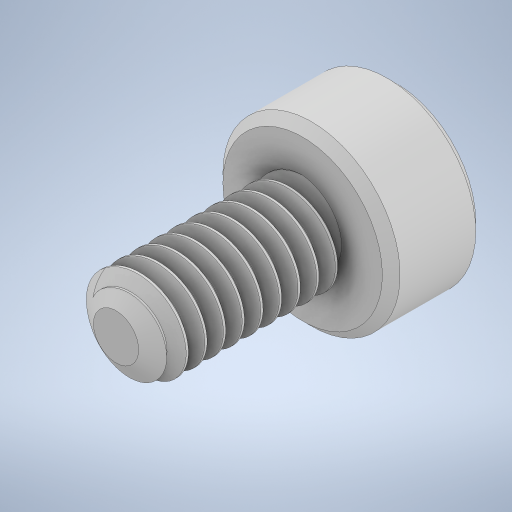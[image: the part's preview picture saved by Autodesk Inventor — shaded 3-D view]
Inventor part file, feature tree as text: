
AUTODESK INVENTOR PART (.ipt)
format: ipt  version: 2024 (Build 280153000, 153)  size: 600,064 bytes
history: native  units: mm
features: other x1, chamfer x1
ambient origin geometry x8: Origin, YZ Plane, XZ Plane, XY Plane, X Axis, Y Axis, Z Axis, Center Point
bodies: Body1 (feature_tree)
feature tree (2):
  other  "Těleso1"
  chamfer  "Chamfer1"  [1 undecoded]
note: 1 required parameter value undecoded (feature->parameter linkage not recoverable at this tier; creation-order binding heuristic only, values carry confidence <= 0.55)
